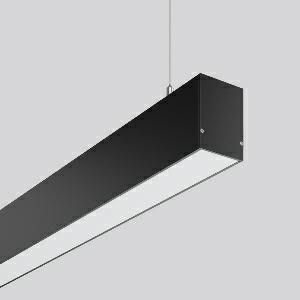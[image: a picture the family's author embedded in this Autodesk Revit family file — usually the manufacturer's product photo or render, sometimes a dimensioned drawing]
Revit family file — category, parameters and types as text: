
# Revit family: less_is_more_50_312320_003_76_5a09
name_source: partatom
category: Lighting Fixtures
units: mm (PartAtom-declared; Revit-internal decimal feet)

## family parameters
Cut with Voids When Loaded = No
Host = Face
Light Source = No
Part Type = Normal
Room Calculation Point = No
Round Connector Dimension = Use Diameter
Shared = No

## types (1)
- LESS IS MORE 50 (1 x LED Modul 830, 6900 lm, 3000)
    Apparent Load = 59 VA
    CIE Flux Codes = 49 80 96 63 100
    Color Rendering = 80
    Color Temperature = 3000
    Default Elevation = 1800 mm
    Description = Series: LESS IS MORE 50
Linear pendant luminaire for aesthetically sophisticated lighting. Housing: extruded aluminium profile, powder-coated. End cap aluminium powder-coated. Canopy made of aluminium, powder-coated. Diffuser made of non-yellowing plastic (PMMA), opal. Direct 65%, indirect 35% light emission. Suitable for pendant. 2-point steel cable suspension freely positionable and infinitely height-adjustable. Special lengths available on request. LED unit with integrated converter interchangeable and removable. Suitable for through-wiring. With sensors or as a safety luminaire on request. 
Colour: deep black, matt (RAL 9005)
Length: 1687 mm
Width: 57 mm
Height: 75 mm
Suspension length: 2000 mm
Lamp: LED
Socket: without socket
Colour temperature: 3000K
Colour rendering index (CRI): 80
Light source: LED
Socket lamp2: Without base
Colour temperature: 3000K
System power: 59 W
Rated luminous flux: 6900 lm
Luminous efficiency: 117 lm/W
Control gear: Converter, dimmable, DALI
Control gear: Converter, dimmable, DALI
Protection class: I
Type of protection: IP 20
    Height = 75 mm
    Lamp = 1 x LED Modul 830
    Lamp Light Flux = 6900 lm
    Lamp count = 1
    Length = 1687 mm
    Lifetime = 50000 h
    Luminous efficacy = 117 lm/W
    Manufacturer = RZB
    ModVariant = No
    Model = 312320.003.76
    Mounting Place = Ceiling
    Mounting Type = Pendant
    Number of Poles = 1
    OnlyDefault = Yes
    Power Factor = 1
    Product Name = LESS IS MORE 50
    Product group = Pendant LED linear luminaires
    ProductGroupID = 907
    Protection Class = Protection class I
    Protection Degree = IP 20
    RLX_Detail_Level = 1
    RLX_Emergency_Light_Flux = 0 lm
    RLX_Emergency_Type = 0
    RLX_Emergency_Type_DB = No
    RlxData = <blob elided: 39845 chars, md5=4b95bf76>
    Socket = socket
    Standby Power = 0 W
    System Light Flux = 6900 lm
    System Power = 59 W
    Type Comments = Product without accessories
    Type Image = 312318.003.jpg
    URL = http://relux.com
    VarID = ---
    Voltage = 230 V
    Voltage Range = 220-240 V
    Weight = 0.00 kg
    Width = 57 mm

## geometry (parser evidence)
native form markers: Blend x4, Sweep x12
no freeform markers — native parametric forms only
